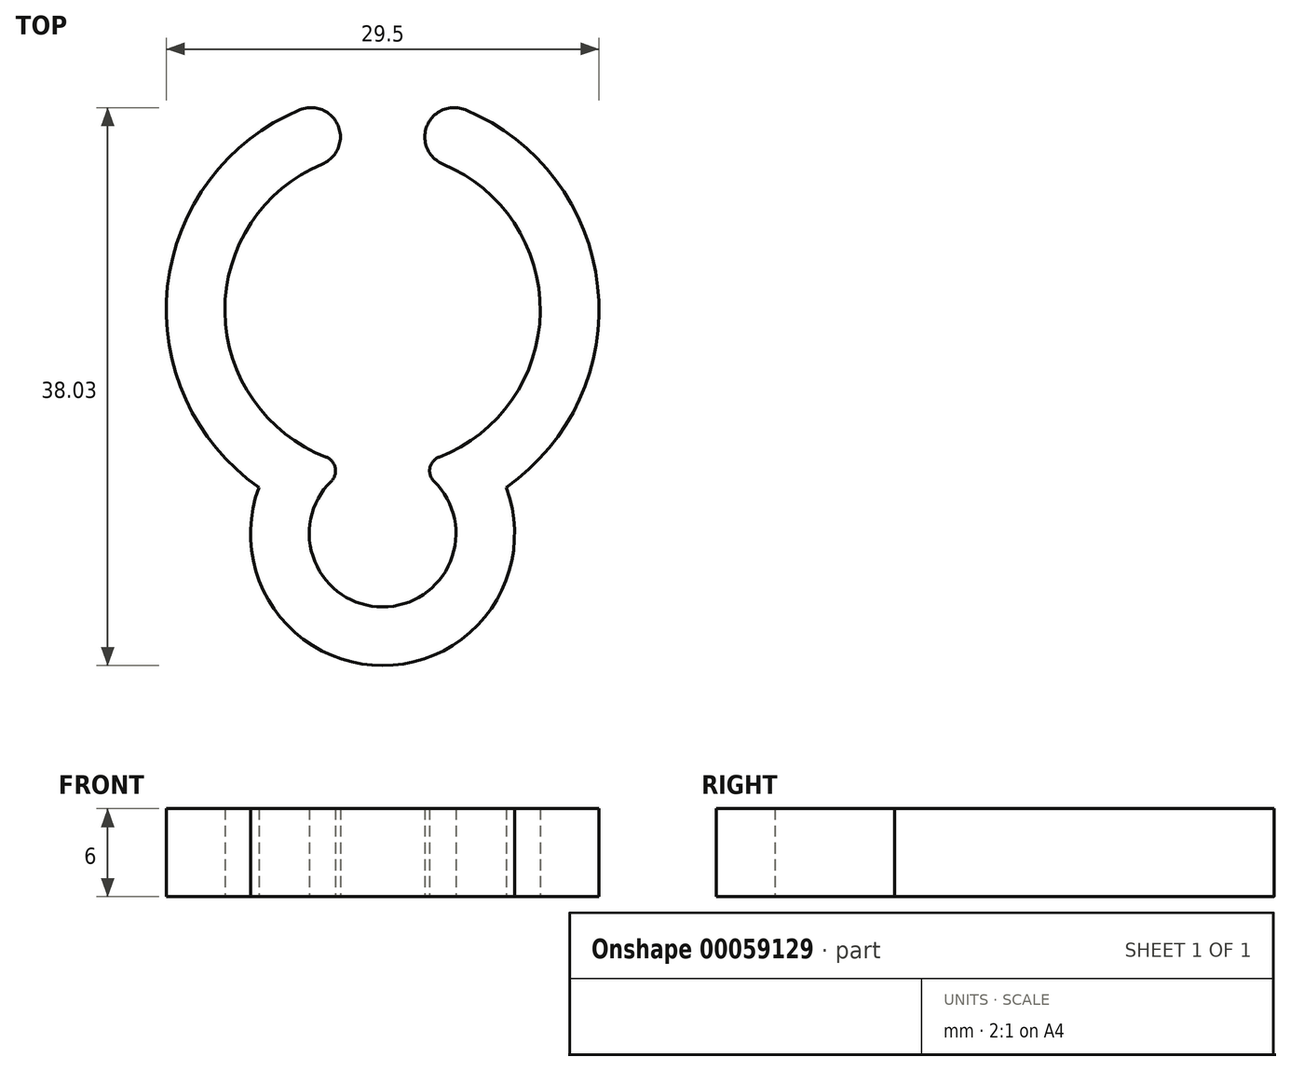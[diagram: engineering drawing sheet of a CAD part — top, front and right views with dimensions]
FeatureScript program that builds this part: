
annotation { "Feature Type Name" : "Feature", "Feature Type Description" : "" }
export const myFeature = defineFeature(function(context is Context, id is Id, definition is map)
    precondition{}
    {
        {
            var Q0;
            Q0=qCreatedBy(makeId("Top.planeOp"),FACE);
            var sketch = newSketch(context, id + "F0", { "sketchPlane" : qUnion([Q0])});
            skArc(sketch, "E0", {"start": v(-4.11, 9.93) * mm, "mid": v(0, 10.75) * mm, "end": v(4.11, 9.93) * mm, "construction": true});
            skLineSegment(sketch, "E1", {"start": v(-4.11, 9.93) * mm, "end": v(0, 0) * mm, "construction": true});
            skLineSegment(sketch, "E2", {"start": v(0, 10.75) * mm, "end": v(0, 0) * mm, "construction": true});
            skLineSegment(sketch, "E3", {"start": v(0, 0) * mm, "end": v(4.11, 9.93) * mm, "construction": true});
            skArc(sketch, "E4", {"start": v(-4.11, 9.93) * mm, "mid": v(-10.75, -0.14) * mm, "end": v(-3.85, -10.04) * mm});
            skArc(sketch, "E5.0", {"start": v(-5.64, 13.63) * mm, "mid": v(-14.66, 1.59) * mm, "end": v(-8.43, -12.1) * mm});
            skLineSegment(sketch, "E6", {"start": v(-5.64, 13.63) * mm, "end": v(-4.11, 9.93) * mm, "construction": true});
            skLineSegment(sketch, "E7", {"start": v(5.64, 13.63) * mm, "end": v(4.11, 9.93) * mm, "construction": true});
            skArc(sketch, "E8", {"start": v(-4.11, 9.93) * mm, "mid": v(-3.03, 12.54) * mm, "end": v(-5.64, 13.63) * mm});
            skArc(sketch, "E9", {"start": v(5.64, 13.63) * mm, "mid": v(3.03, 12.54) * mm, "end": v(4.11, 9.93) * mm});
            skArc(sketch, "E10.0", {"start": v(-5.84, 14.09) * mm, "mid": v(0, -15.25) * mm, "end": v(5.84, 14.09) * mm, "construction": true});
            skArc(sketch, "E11", {"start": v(-3.5, -11.68) * mm, "mid": v(0, -20.25) * mm, "end": v(3.5, -11.68) * mm});
            skArc(sketch, "E12.0", {"start": v(-8.43, -12.1) * mm, "mid": v(0, -24.25) * mm, "end": v(8.43, -12.1) * mm});
            skArc(sketch, "E13.trimOffspring", {"start": v(3.85, -10.04) * mm, "mid": v(10.75, -0.14) * mm, "end": v(4.11, 9.93) * mm});
            skArc(sketch, "E14.trimOffspring", {"start": v(8.43, -12.1) * mm, "mid": v(14.66, 1.59) * mm, "end": v(5.64, 13.63) * mm});
            skPoint(sketch, "E15.visualSharp", {"position": v(-1.82, -10.6) * mm});
            skArc(sketch, "E15.filletArc", {"start": v(-3.5, -11.68) * mm, "mid": v(-3.23, -10.77) * mm, "end": v(-3.85, -10.04) * mm});
            skPoint(sketch, "E16.visualSharp", {"position": v(1.82, -10.6) * mm});
            skArc(sketch, "E16.filletArc", {"start": v(3.85, -10.04) * mm, "mid": v(3.23, -10.77) * mm, "end": v(3.5, -11.68) * mm});
            skSolve(sketch);
        }
        {
            var Q0;
            Q0=makeQuery(id+"F0.imprint","IMPRINT",FACE,{"disambiguationData":[TD([[makeQuery(id+"F0.imprint","IMPRINT",EDGE,{"derivedFrom":sQuery(id+"F0.wireOp",EDGE,"E4")}),-1.0]])]});
            extrude(context, id + "F1", {"entities" : qUnion([Q0]), "depth" : 6 * mm});
        }
    });
